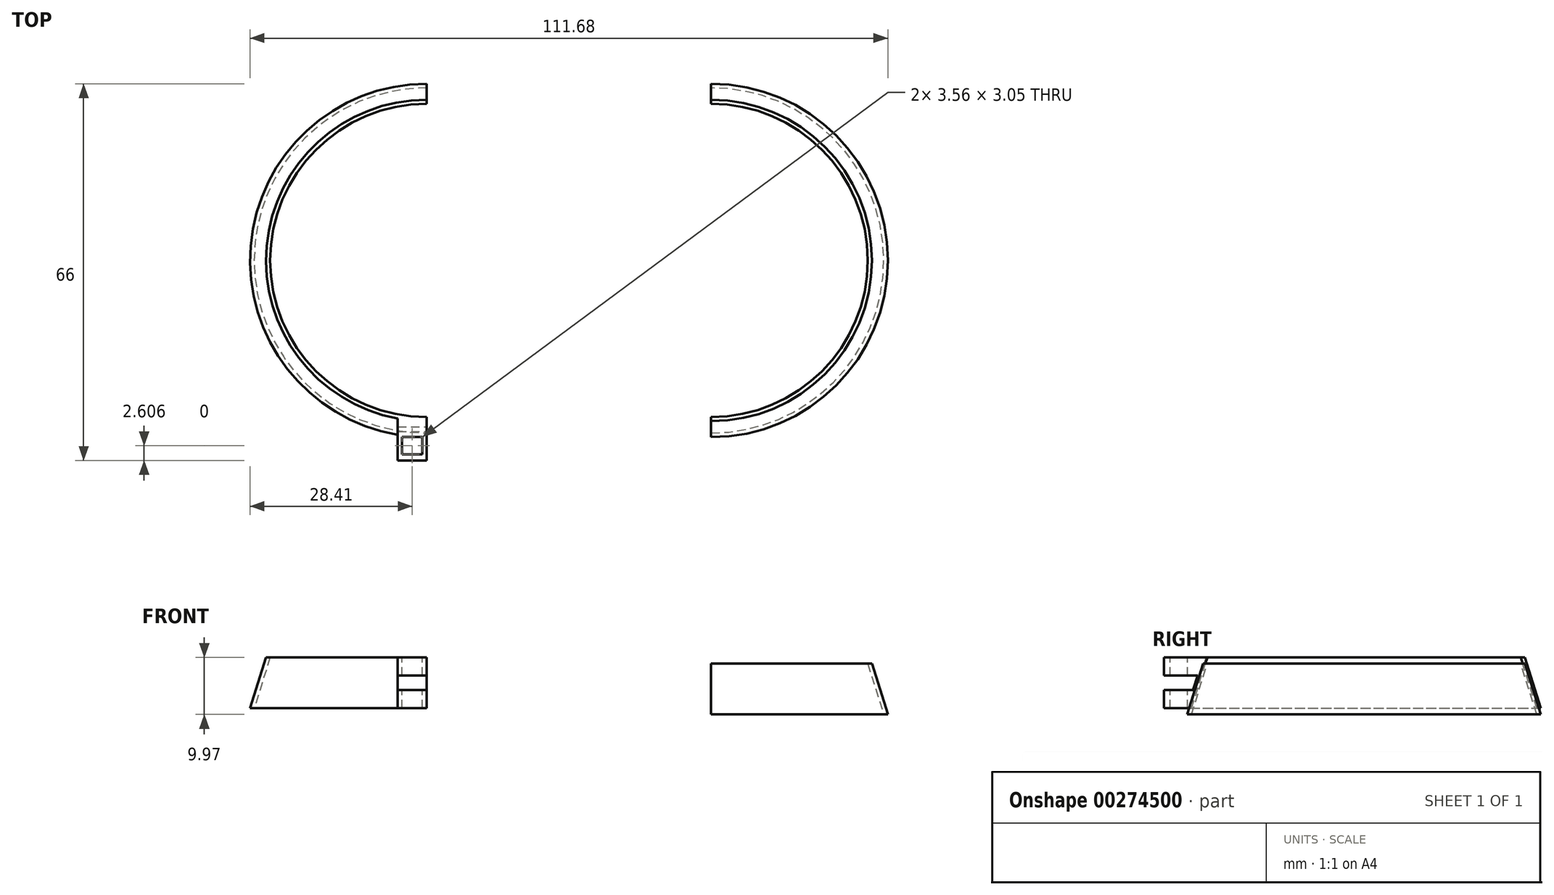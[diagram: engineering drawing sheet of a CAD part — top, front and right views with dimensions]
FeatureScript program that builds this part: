
annotation { "Feature Type Name" : "Feature", "Feature Type Description" : "" }
export const myFeature = defineFeature(function(context is Context, id is Id, definition is map)
    precondition{}
    {
        {
            var Q0;
            Q0=qCreatedBy(makeId("Front.planeOp"),FACE);
            var sketch = newSketch(context, id + "F0", { "sketchPlane" : qUnion([Q0])});
            skLineSegment(sketch, "E0", {"start": v(-63.4, 47.73) * mm, "end": v(-66.2, 38.84) * mm});
            skLineSegment(sketch, "E1", {"start": v(-65.48, 38.84) * mm, "end": v(-62.68, 47.73) * mm});
            skLineSegment(sketch, "E2", {"start": v(-62.68, 47.73) * mm, "end": v(-63.4, 47.73) * mm});
            skLineSegment(sketch, "E3", {"start": v(-35.25, 38.84) * mm, "end": v(-35.25, 47.73) * mm});
            skLineSegment(sketch, "E4", {"start": v(-66.2, 38.84) * mm, "end": v(-65.48, 38.84) * mm});
            skLineSegment(sketch, "E5", {"start": v(-13.63, 46.65) * mm, "end": v(-16.42, 37.76) * mm});
            skLineSegment(sketch, "E6", {"start": v(-15.7, 37.76) * mm, "end": v(-12.9, 46.65) * mm});
            skLineSegment(sketch, "E7", {"start": v(-12.9, 46.65) * mm, "end": v(-13.63, 46.65) * mm});
            skLineSegment(sketch, "E8", {"start": v(14.53, 37.76) * mm, "end": v(14.53, 46.65) * mm});
            skLineSegment(sketch, "E9", {"start": v(-16.42, 37.76) * mm, "end": v(-15.7, 37.76) * mm});
            skSolve(sketch);
        }
        {
            var Q0;
            Q0=makeQuery(id+"F0.imprint","IMPRINT",FACE,{"disambiguationData":[TD([[makeQuery(id+"F0.imprint","IMPRINT",EDGE,{"derivedFrom":sQuery(id+"F0.wireOp",EDGE,"E0")}),1.0]])]});
            var Q1;
            Q1=sQuery(id+"F0.wireOp",EDGE,"E3");
            revolve(context, id + "F1", {"entities" : qUnion([Q0]), "axis" : qUnion([Q1]), "revolveType" : RevolveType.TWO_DIRECTIONS, "angle" : 90 * degree, "angleBack" : 270 * degree});
        }
        {
            var Q0;
            Q0=makeQuery(id+"F0.imprint","IMPRINT",FACE,{"disambiguationData":[TD([[makeQuery(id+"F0.imprint","IMPRINT",EDGE,{"derivedFrom":sQuery(id+"F0.wireOp",EDGE,"E5")}),1.0]])]});
            var Q1;
            Q1=sQuery(id+"F0.wireOp",EDGE,"E8");
            revolve(context, id + "F2", {"entities" : qUnion([Q0]), "axis" : qUnion([Q1]), "revolveType" : RevolveType.TWO_DIRECTIONS, "angle" : 270 * degree, "angleBack" : 90 * degree});
        }
        {
            var Q0;
            Q0=makeQuery(id+"F1.opRevolve","CAP_FACE",FACE,{"disambiguationData":[OSD([sQuery(id+"F0.wireOp",EDGE,"E0"),sQuery(id+"F0.wireOp",EDGE,"E1"),sQuery(id+"F0.wireOp",EDGE,"E2"),sQuery(id+"F0.wireOp",EDGE,"E4")])],"isStart":false});
            var sketch = newSketch(context, id + "F3", { "sketchPlane" : qUnion([Q0])});
            skLineSegment(sketch, "E10", {"start": v(-27.43, 47.73) * mm, "end": v(-35.05, 47.73) * mm});
            skPoint(sketch, "E10.endSnap0", {"position": v(-27.8, 47.73) * mm});
            skLineSegment(sketch, "E11", {"start": v(-35.05, 47.73) * mm, "end": v(-35.05, 38.84) * mm});
            skLineSegment(sketch, "E12", {"start": v(-35.05, 38.84) * mm, "end": v(-30.23, 38.84) * mm});
            skLineSegment(sketch, "E13", {"start": v(-29.55, 43.29) * mm, "end": v(-35.05, 43.29) * mm});
            skLineSegment(sketch, "E14", {"start": v(-35.05, 44.56) * mm, "end": v(-29.15, 44.56) * mm});
            skLineSegment(sketch, "E15", {"start": v(-35.05, 42.02) * mm, "end": v(-29.95, 42.02) * mm});
            skSolve(sketch);
        }
        {
            var Q0;
            {var subQ1=makeQuery(id+"F1.opRevolve","CAP_EDGE",EDGE,{"disambiguationData":[OSD([sQuery(id+"F0.wireOp",EDGE,"E0")])],"isStart":false});Q0=makeQuery(id+"F3.imprint","IMPRINT",FACE,{"disambiguationData":[TD([[makeQuery(id+"F3.imprint","IMPRINT",EDGE,{"derivedFrom":subQ1}),1.0]])]});}
            var Q1;
            {var subQ2=sQuery(id+"F3.wireOp",EDGE,"E11");Q1=makeQuery(id+"F3.imprint","IMPRINT",FACE,{"disambiguationData":[TD([[makeQuery(id+"F3.imprint","IMPRINT",EDGE,{"derivedFrom":subQ2}),1.0]])]});}
            extrude(context, id + "F4", {"entities" : qUnion([Q0, Q1]), "operationType" : NewBodyOperationType.ADD, "oppositeDirection" : true, "depth" : 5.08 * mm});
        }
        {
            var Q0;
            {var subQ0=sQuery(id+"F3.wireOp",EDGE,"E13");Q0=makeQuery(id+"F3.imprint","IMPRINT",FACE,{"disambiguationData":[TD([[makeQuery(id+"F3.imprint","IMPRINT",EDGE,{"derivedFrom":subQ0}),-1.0]])]});}
            var Q1;
            {var subQ0=sQuery(id+"F3.wireOp",EDGE,"E13");Q1=makeQuery(id+"F3.imprint","IMPRINT",FACE,{"disambiguationData":[TD([[makeQuery(id+"F3.imprint","IMPRINT",EDGE,{"derivedFrom":subQ0}),1.0]])]});}
            extrude(context, id + "F5", {"entities" : qUnion([Q0, Q1]), "operationType" : NewBodyOperationType.REMOVE, "oppositeDirection" : true, "depth" : 5.08 * mm});
        }
        {
            var Q0;
            Q0=makeQuery(id+"F4.boolean.opBoolean","MERGE",FACE,{"derivedFrom":[makeQuery(id+"F1.opRevolve","SWEPT_FACE",FACE,{"disambiguationData":[OSD([sQuery(id+"F0.wireOp",EDGE,"E2")])]}),makeQuery(id+"F4.opExtrude","SWEPT_FACE",FACE,{"disambiguationData":[OSD([sQuery(id+"F3.wireOp",EDGE,"E10")])]})]});
            var sketch = newSketch(context, id + "F6", { "sketchPlane" : qUnion([Q0])});
            skPoint(sketch, "E16.middle.positionSnap0", {"position": v(-37.79, -35.05) * mm});
            skPoint(sketch, "E16.middle.positionSnap1", {"position": v(-35.25, -31.24) * mm});
            skPoint(sketch, "E16.centerSnap0", {"position": v(-37.79, -35.05) * mm});
            skPoint(sketch, "E16.centerSnap1", {"position": v(-35.25, -31.24) * mm});
            skLineSegment(sketch, "E17", {"start": v(-39.57, -33.97) * mm, "end": v(-39.57, -30.92) * mm});
            skLineSegment(sketch, "E18", {"start": v(-39.57, -30.92) * mm, "end": v(-36.01, -30.92) * mm});
            skLineSegment(sketch, "E19", {"start": v(-39.57, -33.97) * mm, "end": v(-36.01, -33.97) * mm});
            skLineSegment(sketch, "E20", {"start": v(-36.01, -33.97) * mm, "end": v(-36.01, -30.92) * mm});
            skSolve(sketch);
        }
        {
            var Q0;
            Q0=makeQuery(id+"F6.imprint","IMPRINT",FACE,{"disambiguationData":[TD([[makeQuery(id+"F6.imprint","IMPRINT",EDGE,{"derivedFrom":sQuery(id+"F6.wireOp",EDGE,"E17")}),-1.0]])]});
            extrude(context, id + "F7", {"entities" : qUnion([Q0]), "operationType" : NewBodyOperationType.REMOVE, "oppositeDirection" : true, "depth" : 25.4 * mm});
        }
    });
